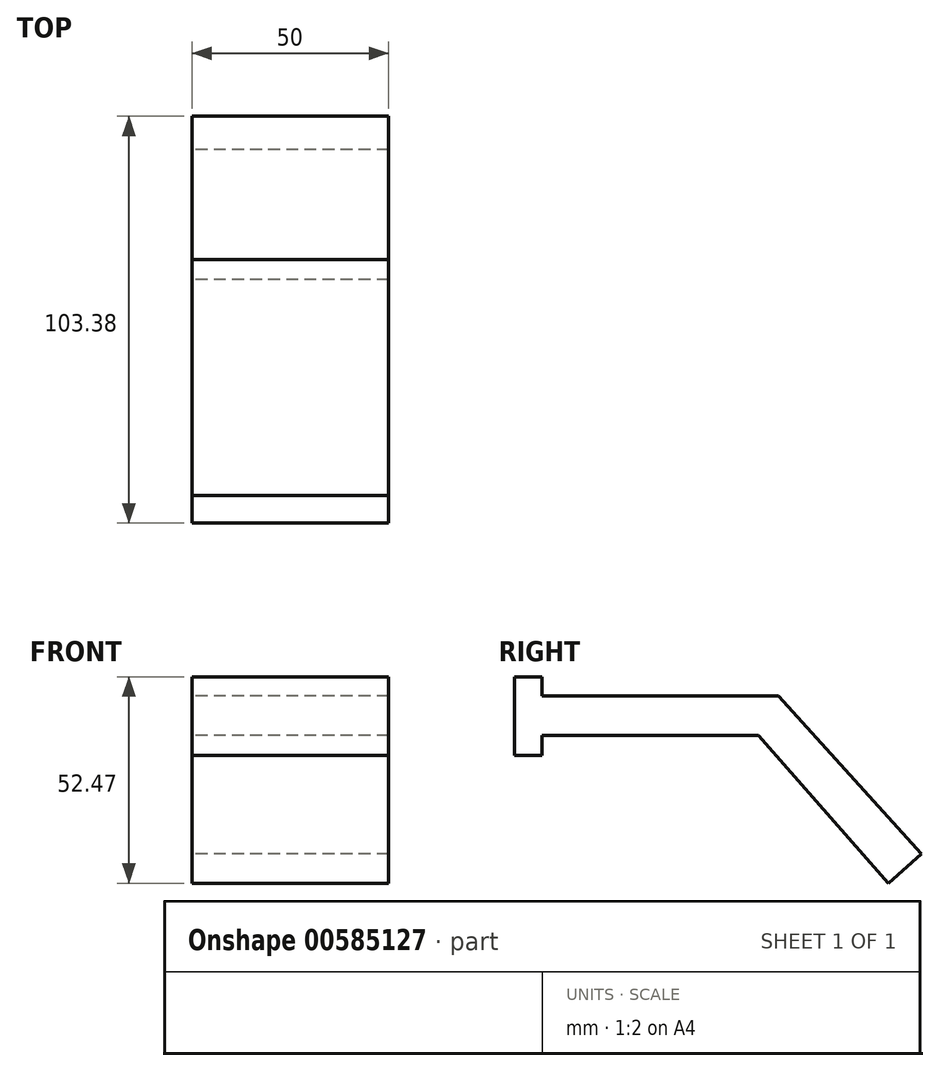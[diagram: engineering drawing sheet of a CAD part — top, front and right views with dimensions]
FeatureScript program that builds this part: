
annotation { "Feature Type Name" : "Feature", "Feature Type Description" : "" }
export const myFeature = defineFeature(function(context is Context, id is Id, definition is map)
    precondition{}
    {
        {
            var Q0;
            Q0=qCreatedBy(makeId("Right.planeOp"),FACE);
            var sketch = newSketch(context, id + "F0", { "sketchPlane" : qUnion([Q0])});
            skLineSegment(sketch, "E0", {"start": v(-42.08, 21.79) * mm, "end": v(-42.08, 31.79) * mm});
            skLineSegment(sketch, "E1.bottom", {"start": v(-49.08, 36.7) * mm, "end": v(-42.08, 36.7) * mm});
            skLineSegment(sketch, "E1.top", {"start": v(-49.08, 16.7) * mm, "end": v(-42.08, 16.7) * mm});
            skLineSegment(sketch, "E1.left", {"start": v(-49.08, 36.7) * mm, "end": v(-49.08, 16.7) * mm});
            skLineSegment(sketch, "E1.right", {"start": v(-42.08, 36.7) * mm, "end": v(-42.08, 16.7) * mm});
            skLineSegment(sketch, "E2", {"start": v(-42.08, 31.79) * mm, "end": v(17.92, 31.79) * mm});
            skLineSegment(sketch, "E3", {"start": v(17.92, 31.79) * mm, "end": v(12.88, 21.79) * mm});
            skLineSegment(sketch, "E4", {"start": v(12.88, 21.79) * mm, "end": v(-42.08, 21.79) * mm});
            skLineSegment(sketch, "E5", {"start": v(12.88, 21.79) * mm, "end": v(45.88, -15.77) * mm});
            skLineSegment(sketch, "E6", {"start": v(45.88, -15.77) * mm, "end": v(54.3, -8.38) * mm});
            skLineSegment(sketch, "E7", {"start": v(54.3, -8.38) * mm, "end": v(17.92, 31.79) * mm});
            skSolve(sketch);
        }
        {
            var Q0;
            Q0=makeQuery(id+"F0.imprint","IMPRINT",FACE,{"disambiguationData":[TD([[makeQuery(id+"F0.imprint","IMPRINT",EDGE,{"derivedFrom":sQuery(id+"F0.wireOp",EDGE,"E3")}),1.0]])]});
            var Q1;
            {var subQ0=sQuery(id+"F0.wireOp",EDGE,"E2");Q1=makeQuery(id+"F0.imprint","IMPRINT",FACE,{"disambiguationData":[TD([[makeQuery(id+"F0.imprint","IMPRINT",EDGE,{"derivedFrom":subQ0}),-1.0]])]});}
            var Q2;
            {var subQ1=sQuery(id+"F0.wireOp",EDGE,"E1.bottom");Q2=makeQuery(id+"F0.imprint","IMPRINT",FACE,{"disambiguationData":[TD([[makeQuery(id+"F0.imprint","IMPRINT",EDGE,{"derivedFrom":subQ1}),-1.0]])]});}
            extrude(context, id + "F1", {"entities" : qUnion([Q0, Q1, Q2]), "depth" : 50 * mm, "offsetDistance" : 25 * mm});
        }
    });
